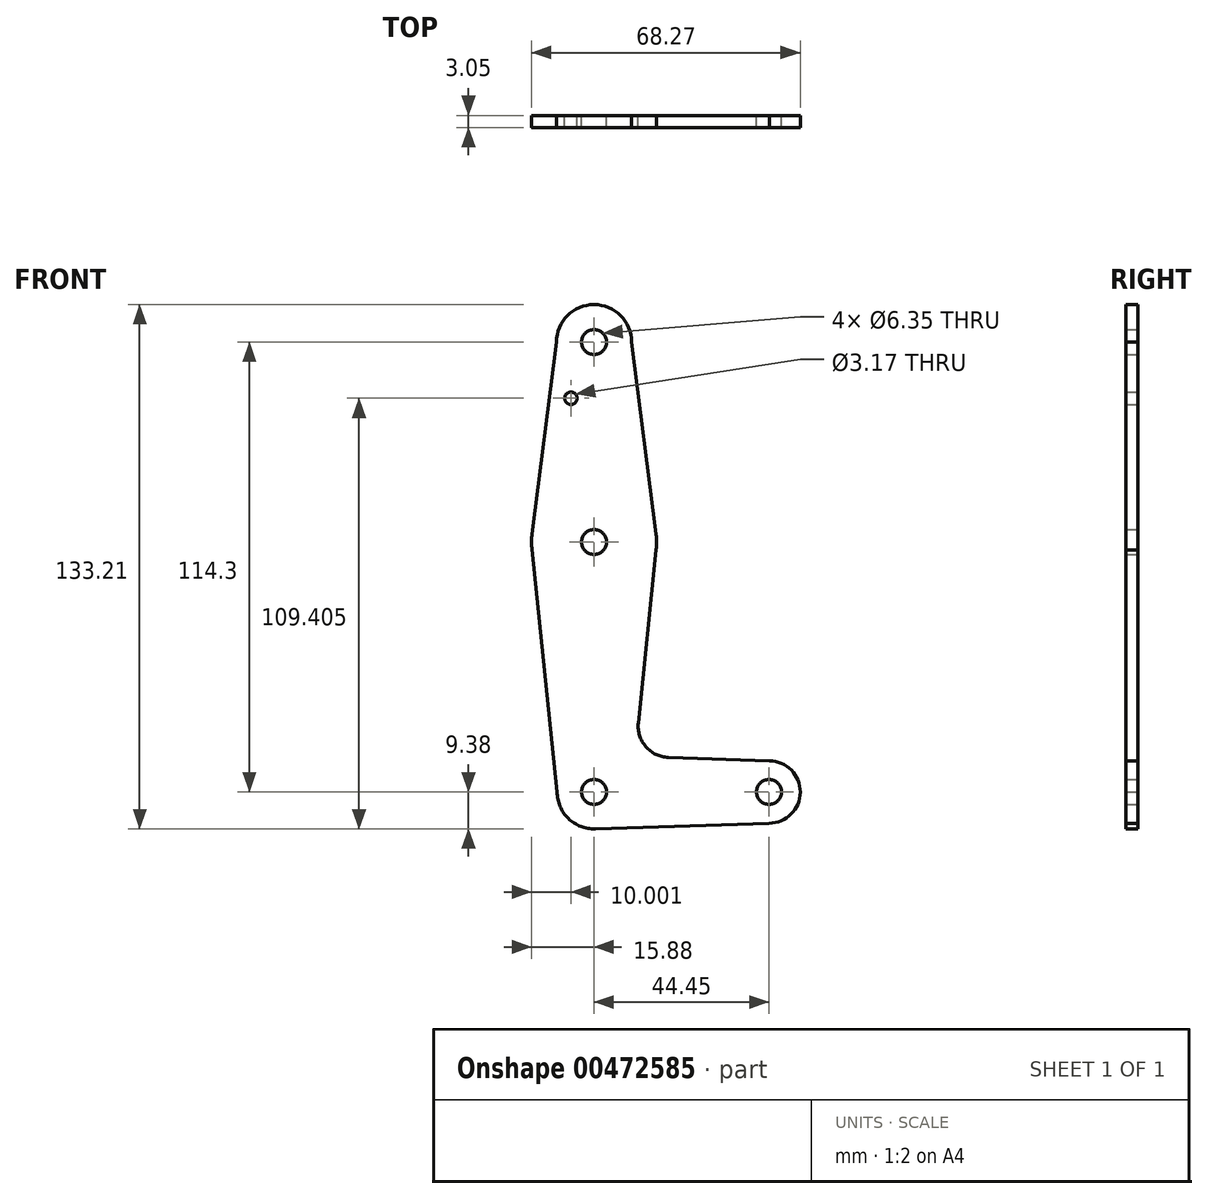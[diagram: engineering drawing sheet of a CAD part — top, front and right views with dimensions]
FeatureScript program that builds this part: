
annotation { "Feature Type Name" : "Feature", "Feature Type Description" : "" }
export const myFeature = defineFeature(function(context is Context, id is Id, definition is map)
    precondition{}
    {
        {
            var Q0;
            Q0=qCreatedBy(makeId("Front.planeOp"),FACE);
            var sketch = newSketch(context, id + "F0", { "sketchPlane" : qUnion([Q0])});
            skLineSegment(sketch, "E0", {"start": v(0, 114.3) * mm, "end": v(0, 0) * mm, "construction": true});
            skLineSegment(sketch, "E1", {"start": v(0, 0) * mm, "end": v(44.45, 0) * mm});
            skCircle(sketch, "E2", {"center": v(44.45, 0) * mm, "radius": 7.94 * mm});
            skCircle(sketch, "E3", {"center": v(0, 0) * mm, "radius": 9.38 * mm});
            skCircle(sketch, "E4", {"center": v(0, 114.3) * mm, "radius": 9.53 * mm});
            skCircle(sketch, "E5", {"center": v(0, 63.5) * mm, "radius": 15.88 * mm});
            skLineSegment(sketch, "E6", {"start": v(-9.53, 114.3) * mm, "end": v(-15.75, 65.5) * mm});
            skLineSegment(sketch, "E7", {"start": v(9.52, 114.3) * mm, "end": v(15.75, 65.5) * mm});
            skLineSegment(sketch, "E8", {"start": v(15.75, 61.5) * mm, "end": v(11.23, 17.53) * mm});
            skLineSegment(sketch, "E9", {"start": v(44.44, -7.94) * mm, "end": v(0.3, -9.38) * mm});
            skLineSegment(sketch, "E10", {"start": v(44.55, 7.94) * mm, "end": v(18.88, 8.77) * mm});
            skCircle(sketch, "E11", {"center": v(0, 114.3) * mm, "radius": 3.18 * mm});
            skCircle(sketch, "E12", {"center": v(0, 63.5) * mm, "radius": 3.18 * mm});
            skCircle(sketch, "E13", {"center": v(0, 0) * mm, "radius": 3.18 * mm});
            skCircle(sketch, "E14", {"center": v(44.45, 0) * mm, "radius": 3.18 * mm});
            skCircle(sketch, "E15", {"center": v(-5.88, 100.03) * mm, "radius": 1.59 * mm});
            skArc(sketch, "E16.filletArc", {"start": v(11.23, 17.53) * mm, "mid": v(13.15, 11.49) * mm, "end": v(18.88, 8.77) * mm});
            skLineSegment(sketch, "E17", {"start": v(-15.82, 62.14) * mm, "end": v(-9.38, 0) * mm});
            skSolve(sketch);
        }
        {
            var Q0;
            Q0 = qSketchRegion(id + "F0", true);
            extrude(context, id + "F1", {"entities" : qUnion([Q0]), "depth" : 3.05 * mm});
        }
    });
